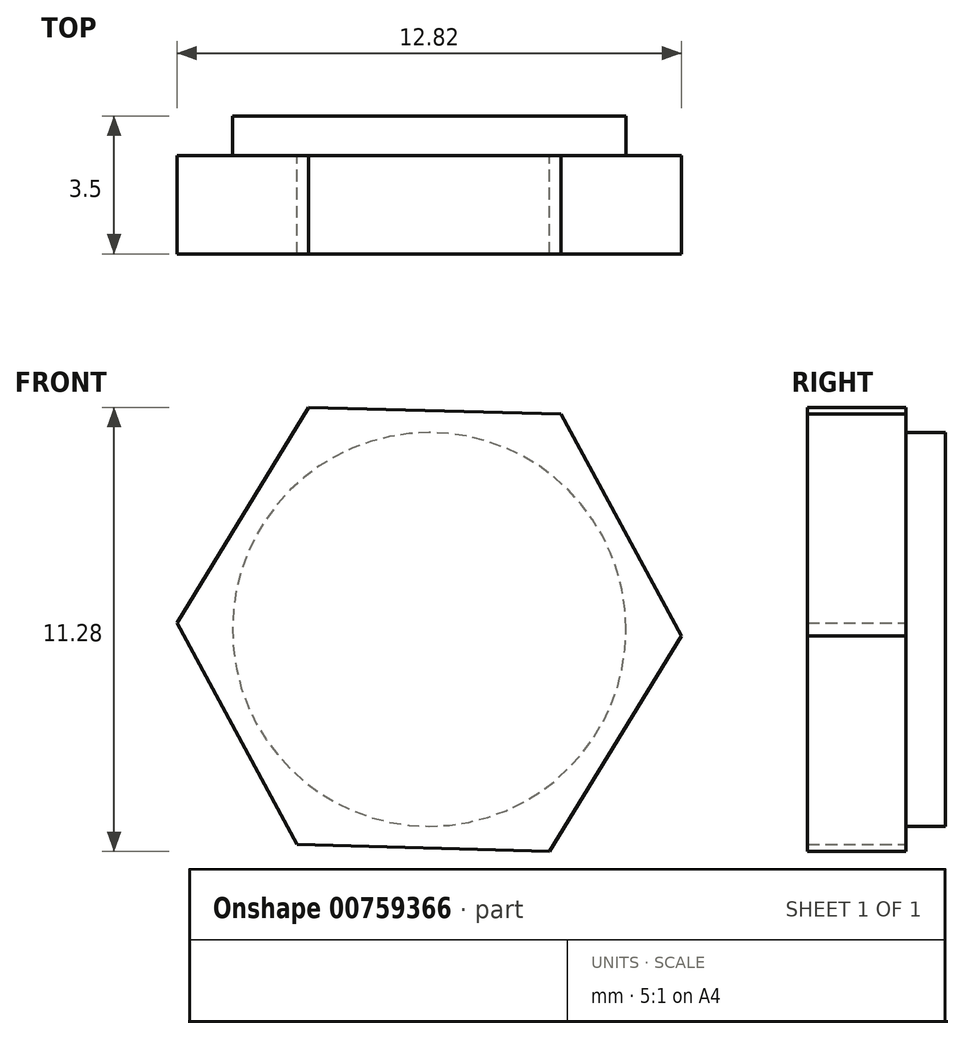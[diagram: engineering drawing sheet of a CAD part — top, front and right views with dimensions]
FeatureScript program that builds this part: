
annotation { "Feature Type Name" : "Feature", "Feature Type Description" : "" }
export const myFeature = defineFeature(function(context is Context, id is Id, definition is map)
    precondition{}
    {
        {
            var Q0;
            Q0=qCreatedBy(makeId("Front.planeOp"),FACE);
            var sketch = newSketch(context, id + "F0", { "sketchPlane" : qUnion([Q0])});
            skCircle(sketch, "E0.cCircle", {"center": v(0, 0) * mm, "radius": 5.55 * mm, "construction": true});
            skLineSegment(sketch, "E0.0", {"start": v(-6.41, 0.17) * mm, "end": v(-3.06, 5.64) * mm});
            skLineSegment(sketch, "E0.1", {"start": v(-3.06, 5.64) * mm, "end": v(3.35, 5.47) * mm});
            skLineSegment(sketch, "E0.2", {"start": v(3.35, 5.47) * mm, "end": v(6.41, -0.17) * mm});
            skLineSegment(sketch, "E0.3", {"start": v(6.41, -0.17) * mm, "end": v(3.06, -5.64) * mm});
            skLineSegment(sketch, "E0.4", {"start": v(3.06, -5.64) * mm, "end": v(-3.35, -5.47) * mm});
            skLineSegment(sketch, "E0.5", {"start": v(-3.35, -5.47) * mm, "end": v(-6.41, 0.17) * mm});
            skPoint(sketch, "E0.0.midPoint", {"position": v(-4.74, 2.9) * mm});
            skCircle(sketch, "E1", {"center": v(0, 0) * mm, "radius": 5 * mm});
            skSolve(sketch);
        }
        {
            var Q0;
            Q0 = qSketchRegion(id + "F0", true);
            var Q1;
            Q1=makeQuery(id+"F0.imprint","IMPRINT",FACE,{"disambiguationData":[TD([[makeQuery(id+"F0.imprint","IMPRINT",EDGE,{"derivedFrom":sQuery(id+"F0.wireOp",EDGE,"E1")}),1.0]])]});
            extrude(context, id + "F1", {"entities" : qUnion([Q0, Q1]), "depth" : 2.5 * mm, "offsetDistance" : 25 * mm});
        }
        {
            var Q0;
            Q0=makeQuery(id+"F0.imprint","IMPRINT",FACE,{"disambiguationData":[TD([[makeQuery(id+"F0.imprint","IMPRINT",EDGE,{"derivedFrom":sQuery(id+"F0.wireOp",EDGE,"E1")}),1.0]])]});
            extrude(context, id + "F2", {"entities" : qUnion([Q0]), "operationType" : NewBodyOperationType.ADD, "oppositeDirection" : true, "depth" : 1 * mm, "offsetDistance" : 25 * mm});
        }
    });
